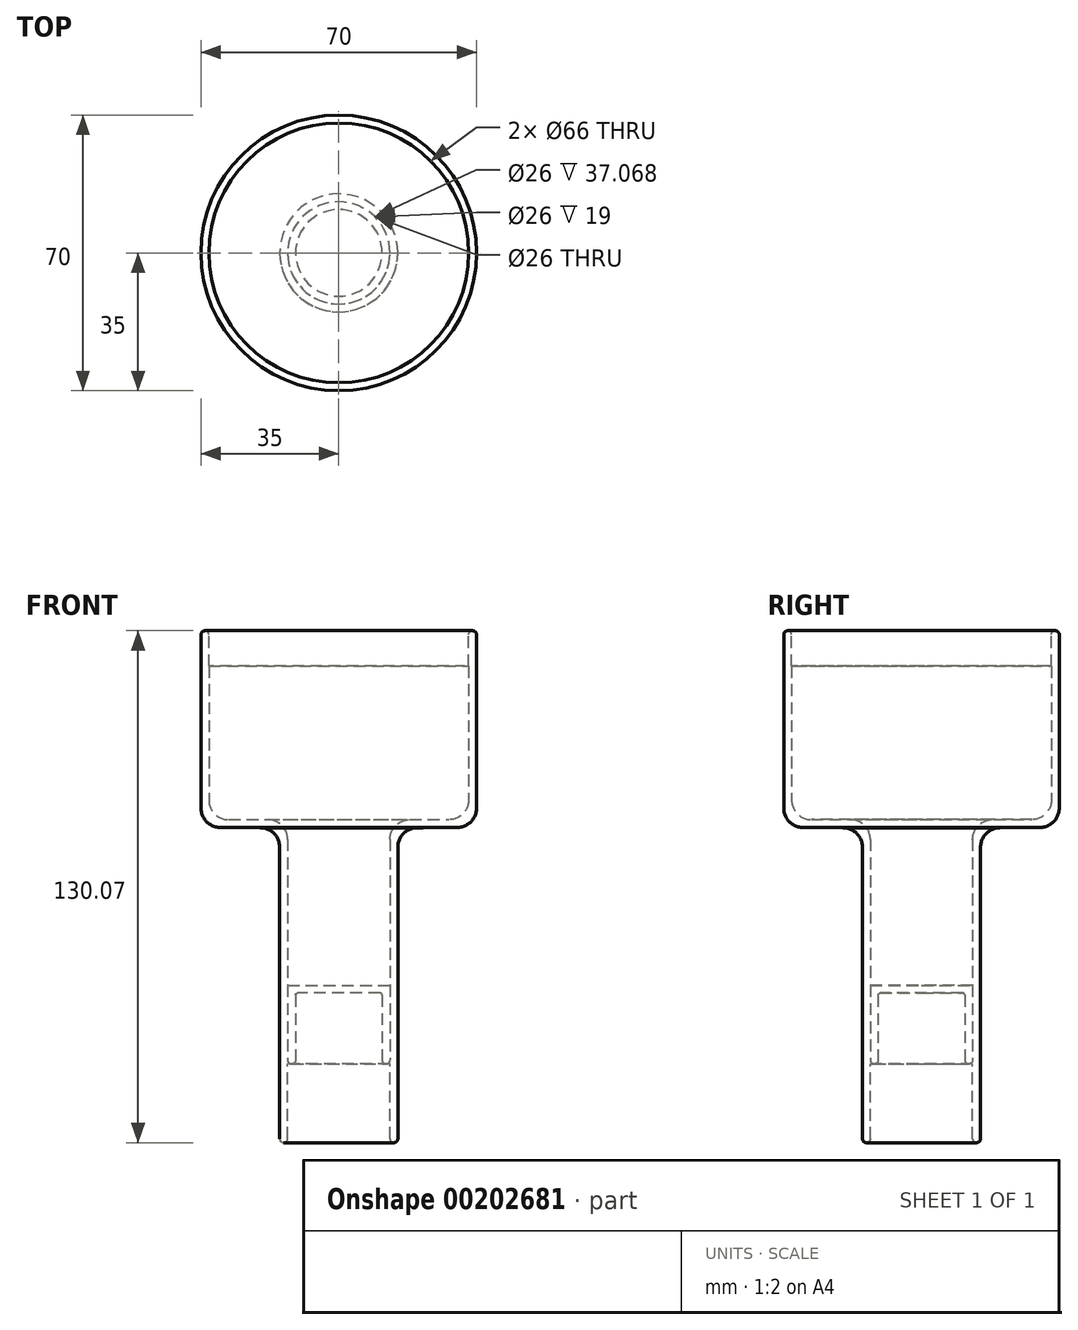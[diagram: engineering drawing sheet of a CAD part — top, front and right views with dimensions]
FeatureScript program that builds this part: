
annotation { "Feature Type Name" : "Feature", "Feature Type Description" : "" }
export const myFeature = defineFeature(function(context is Context, id is Id, definition is map)
    precondition{}
    {
        {
            var Q0;
            Q0=qCreatedBy(makeId("Front.planeOp"),FACE);
            var sketch = newSketch(context, id + "F0", { "sketchPlane" : qUnion([Q0])});
            skLineSegment(sketch, "E0", {"start": v(0, -80.07) * mm, "end": v(0, 49.93) * mm});
            skLineSegment(sketch, "E1", {"start": v(-13, -80.07) * mm, "end": v(-15, -80.07) * mm});
            skLineSegment(sketch, "E2", {"start": v(-15, -80.07) * mm, "end": v(-15, -0.07) * mm});
            skLineSegment(sketch, "E3", {"start": v(-15, -0.07) * mm, "end": v(-35, 0) * mm});
            skLineSegment(sketch, "E4", {"start": v(-35, 0) * mm, "end": v(-35, 50) * mm});
            skLineSegment(sketch, "E5", {"start": v(-35, 50) * mm, "end": v(-33, 50) * mm});
            skLineSegment(sketch, "E6.4", {"start": v(-7.2, -72.88) * mm, "end": v(-7.8, -72.88) * mm});
            skLineSegment(sketch, "E7.0", {"start": v(-33, 41.02) * mm, "end": v(-33, 50) * mm});
            skLineSegment(sketch, "E7.2", {"start": v(-13, -80.07) * mm, "end": v(-13, -60.07) * mm});
            skPoint(sketch, "E8.endSnap0", {"position": v(-13, -39.07) * mm});
            skPoint(sketch, "E9.orphan", {"position": v(-13, 1.93) * mm});
            skSolve(sketch);
        }
        {
            var Q0;
            Q0=sQuery(id+"F0.wireOp",EDGE,"E7.2");
            var Q1;
            Q1=sQuery(id+"F0.wireOp",EDGE,"E1");
            var Q2;
            Q2=sQuery(id+"F0.wireOp",EDGE,"E2");
            var Q3;
            Q3=sQuery(id+"F0.wireOp",EDGE,"E3");
            var Q4;
            Q4=sQuery(id+"F0.wireOp",EDGE,"E4");
            var Q5;
            Q5=sQuery(id+"F0.wireOp",EDGE,"E5");
            var Q6;
            Q6=sQuery(id+"F0.wireOp",EDGE,"E7.0");
            var Q7;
            Q7=sQuery(id+"F0.wireOp",EDGE,"E0");
            revolve(context, id + "F1", {"bodyType" : ToolBodyType.SURFACE, "surfaceEntities" : qUnion([Q0, Q1, Q2, Q3, Q4, Q5, Q6]), "axis" : qUnion([Q7]), "revolveType" : RevolveType.FULL});
        }
        {
            var Q0;
            Q0=qCreatedBy(makeId("Front.planeOp"),FACE);
            var sketch = newSketch(context, id + "F2", { "sketchPlane" : qUnion([Q0])});
            skLineSegment(sketch, "E10.0", {"start": v(-13, -60.07) * mm, "end": v(-11, -60.07) * mm});
            skLineSegment(sketch, "E11.top", {"start": v(-13, -40.07) * mm, "end": v(0, -40.07) * mm});
            skLineSegment(sketch, "E11.left", {"start": v(-13, -60.07) * mm, "end": v(-13, -40.07) * mm});
            skLineSegment(sketch, "E12.1", {"start": v(-11, -42.07) * mm, "end": v(0, -42.07) * mm});
            skLineSegment(sketch, "E12.2", {"start": v(-11, -60.07) * mm, "end": v(-11, -42.07) * mm});
            skLineSegment(sketch, "E13", {"start": v(0, -40.07) * mm, "end": v(0, -60.07) * mm});
            skPoint(sketch, "E11.right.end.orphan", {"position": v(13, -40.07) * mm});
            skPoint(sketch, "E14.orphan", {"position": v(13, -60.07) * mm});
            skSolve(sketch);
        }
        {
            var Q0;
            Q0 = qSketchRegion(id + "F2", true);
            var Q1;
            Q1=sQuery(id+"F2.wireOp",EDGE,"E12.1");
            var Q2;
            Q2=sQuery(id+"F2.wireOp",EDGE,"E11.top");
            var Q3;
            Q3=sQuery(id+"F2.wireOp",EDGE,"E11.left");
            var Q4;
            Q4=sQuery(id+"F2.wireOp",EDGE,"E12.2");
            var Q5;
            Q5=sQuery(id+"F2.wireOp",EDGE,"E10.0");
            var Q6;
            Q6=sQuery(id+"F2.wireOp",EDGE,"E13");
            revolve(context, id + "F3", {"bodyType" : ToolBodyType.SURFACE, "entities" : qUnion([Q0]), "surfaceEntities" : qUnion([Q1, Q2, Q3, Q4, Q5]), "axis" : qUnion([Q6]), "revolveType" : RevolveType.FULL});
        }
        {
            var Q0;
            Q0=qCreatedBy(makeId("Front.planeOp"),FACE);
            var sketch = newSketch(context, id + "F4", { "sketchPlane" : qUnion([Q0])});
            skLineSegment(sketch, "E15.0", {"start": v(0, -40.07) * mm, "end": v(-13, -40.07) * mm});
            skLineSegment(sketch, "E16.0", {"start": v(33, 41.02) * mm, "end": v(0, 41.02) * mm});
            skLineSegment(sketch, "E17", {"start": v(-33, 41.02) * mm, "end": v(-33, 7) * mm});
            skLineSegment(sketch, "E18", {"start": v(0, 0) * mm, "end": v(0, -40.07) * mm});
            skLineSegment(sketch, "E19.0", {"start": v(-28, 2) * mm, "end": v(-18, 2) * mm});
            skPoint(sketch, "E20.orphan", {"position": v(-33, 0) * mm});
            skLineSegment(sketch, "E21", {"start": v(-13, -40.07) * mm, "end": v(-13, -3) * mm});
            skLineSegment(sketch, "E22", {"start": v(0, 41.02) * mm, "end": v(0, 0) * mm});
            skPoint(sketch, "E23.orphan", {"position": v(13, -40.07) * mm});
            skPoint(sketch, "E24.visualSharp", {"position": v(-33, 2) * mm});
            skArc(sketch, "E24.filletArc", {"start": v(-33, 7) * mm, "mid": v(-31.54, 3.46) * mm, "end": v(-28, 2) * mm});
            skPoint(sketch, "E25.visualSharp", {"position": v(-13, 2) * mm});
            skArc(sketch, "E25.filletArc", {"start": v(-13, -3) * mm, "mid": v(-14.46, 0.54) * mm, "end": v(-18, 2) * mm});
            skSolve(sketch);
        }
        {
            var Q0;
            Q0=sQuery(id+"F4.wireOp",EDGE,"E17");
            var Q1;
            Q1=sQuery(id+"F4.wireOp",EDGE,"E24.filletArc");
            var Q2;
            Q2=sQuery(id+"F4.wireOp",EDGE,"E19.0");
            var Q3;
            Q3=sQuery(id+"F4.wireOp",EDGE,"E25.filletArc");
            var Q4;
            Q4=sQuery(id+"F4.wireOp",EDGE,"E21");
            var Q5;
            Q5=sQuery(id+"F4.wireOp",EDGE,"E15.0");
            var Q6;
            Q6=sQuery(id+"F4.wireOp",EDGE,"E22");
            revolve(context, id + "F5", {"bodyType" : ToolBodyType.SURFACE, "surfaceEntities" : qUnion([Q0, Q1, Q2, Q3, Q4, Q5]), "axis" : qUnion([Q6]), "revolveType" : RevolveType.FULL});
        }
        {
            var Q0;
            Q0=makeQuery(id+"F1.opRevolve","SWEPT_EDGE",EDGE,{"disambiguationData":[OSD([sQuery(id+"F0.wireOp",VERTEX,"E4.start")])]});
            var Q1;
            Q1=makeQuery(id+"F1.opRevolve","SWEPT_EDGE",EDGE,{"disambiguationData":[OSD([sQuery(id+"F0.wireOp",VERTEX,"E3.start")])]});
            fillet(context, id + "F6", {"entities" : qUnion([Q0, Q1]), "radius" : 5 * mm, "tangentPropagation" : true, "allowEdgeOverflow" : false});
        }
        {
            var Q0;
            Q0=qCreatedBy(makeId("Front.planeOp"),FACE);
            var sketch = newSketch(context, id + "F7", { "sketchPlane" : qUnion([Q0])});
            skLineSegment(sketch, "E26.0", {"start": v(0, 41.02) * mm, "end": v(-33, 41.02) * mm});
            skLineSegment(sketch, "E27", {"start": v(0, 41.02) * mm, "end": v(0, 29.8) * mm});
            skPoint(sketch, "E27.endSnap0", {"position": v(0, 41.02) * mm});
            skPoint(sketch, "E28.orphan", {"position": v(33, 41.02) * mm});
            skSolve(sketch);
        }
        {
            var Q0;
            Q0 = qSketchRegion(id + "F7", true);
            var Q1;
            Q1=sQuery(id+"F7.wireOp",EDGE,"E26.0");
            var Q2;
            Q2=sQuery(id+"F7.wireOp",EDGE,"E27");
            revolve(context, id + "F8", {"bodyType" : ToolBodyType.SURFACE, "entities" : qUnion([Q0]), "surfaceEntities" : qUnion([Q1]), "axis" : qUnion([Q2]), "revolveType" : RevolveType.FULL});
        }
        {
            var Q0;
            Q0=makeQuery(id+"F1.opRevolve","SWEPT_FACE",FACE,{"disambiguationData":[OSD([sQuery(id+"F0.wireOp",EDGE,"E5")])]});
            var Q1;
            Q1=makeQuery(id+"F1.opRevolve","SWEPT_FACE",FACE,{"disambiguationData":[OSD([sQuery(id+"F0.wireOp",EDGE,"E1")])]});
            var Q2;
            Q2=makeQuery(id+"F3.opRevolve","SWEPT_FACE",FACE,{"disambiguationData":[OSD([sQuery(id+"F2.wireOp",EDGE,"E10.0")])]});
            fillet(context, id + "F9", {"entities" : qUnion([Q0, Q1, Q2]), "radius" : 1 * mm, "tangentPropagation" : true, "allowEdgeOverflow" : false});
        }
        {
            var Q0;
            Q0=makeQuery(id+"F3.opRevolve","SWEPT_EDGE",EDGE,{"disambiguationData":[OSD([sQuery(id+"F2.wireOp",VERTEX,"E12.2.end")])]});
            fillet(context, id + "F10", {"entities" : qUnion([Q0]), "radius" : 0.5 * mm, "tangentPropagation" : true, "allowEdgeOverflow" : false});
        }
    });
